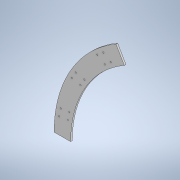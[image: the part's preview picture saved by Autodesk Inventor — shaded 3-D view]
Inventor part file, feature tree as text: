
AUTODESK INVENTOR PART (.ipt)
format: ipt  version: 2020.3 (Build 243373000, 373)  size: 149,504 bytes
history: native  units: mm
features: extrude x3, pattern_circular x1, sketch x1
ambient origin geometry x8: Origin, YZ Plane, XZ Plane, XY Plane, X Axis, Y Axis, Z Axis, Center Point
bodies: Solid1 (feature_tree)
feature tree (5):
  extrude  "Extrusion1"  Depth=10.0mm
  extrude  "Extrusion2"  Depth=4.0mm TaperAngle=0.0deg
  extrude  "Extrusion3"  Depth=10.0mm TaperAngle=0.0deg
  pattern_circular  "Circular Pattern1"  [2 undecoded]
  sketch  "Sketch1"  dims[d0=600.0mm d1=40.0mm d2=4.0mm d3=0.0mm d4=10.0mm d5=0.0mm d6=3.0mm d7=3.0mm d9=270.0mm d11=3.0mm d12=3.0mm d14=270.0mm d16=0.0mm d17=0.0mm d18=90.0mm d19=27.925268mm d21=19.024089mm d22=20.0mm d23=1.396263mm d24=2.094395mm d25=60.0deg]
note: 2 required parameter values undecoded (feature->parameter linkage not recoverable at this tier; creation-order binding heuristic only, values carry confidence <= 0.55)
